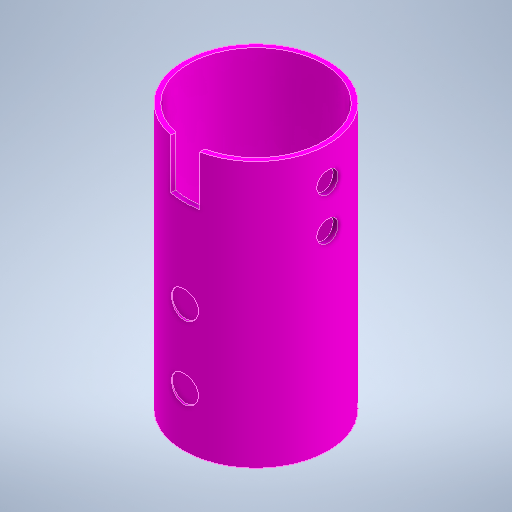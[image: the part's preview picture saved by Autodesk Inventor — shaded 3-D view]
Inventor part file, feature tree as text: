
AUTODESK INVENTOR PART (.ipt)
format: ipt  version: 2025.1 (Build 291241000, 241)  size: 276,480 bytes
history: native  units: mm
features: sketch x4, plane x3, extrude x2, hole x2, projected_geometry x2
ambient origin geometry x8: Origin, YZ Plane, XZ Plane, XY Plane, X Axis, Y Axis, Z Axis, Center Point
bodies: Solid1 (feature_tree)
feature tree (13):
  extrude  "Extrusion1"  Depth=138.0mm TaperAngle=0.0deg
  plane  "Work Plane2"
  extrude  "Extrusion2"  Depth=138.0mm TaperAngle=0.0deg
  plane  "Work Plane3"
  hole  "Hole1"  [1 undecoded]
  plane  "Work Plane4"
  hole  "Hole2"  [1 undecoded]
  sketch  "Sketch1"  dims[d1=70.0mm d2=138.0mm d3=0.0mm]
  sketch  "Sketch2"  dims[d5=-40.0mm d8=138.0mm d9=0.0mm]
  projected_geometry  "Projected Loop1"
  sketch  "Sketch3"  dims[d10=37.5mm d11=22.0mm]
  projected_geometry  "Projected Loop2"
  sketch  "Sketch4"  dims[d12=17.0mm d13=11.0mm d14=6.0mm d15=4.0mm d16=2.0mm d17=90.0deg d18=3.0mm d19=0.0mm d20=-40.0mm d21=38.0mm d23=14.0mm d24=6.0mm d25=4.0mm d26=2.0mm d27=90.0deg d28=3.5mm d29=0.0mm d33=15.0mm d34=26.0mm d35=28.0mm d36=75.0mm]
note: 2 required parameter values undecoded (feature->parameter linkage not recoverable at this tier; creation-order binding heuristic only, values carry confidence <= 0.55)
